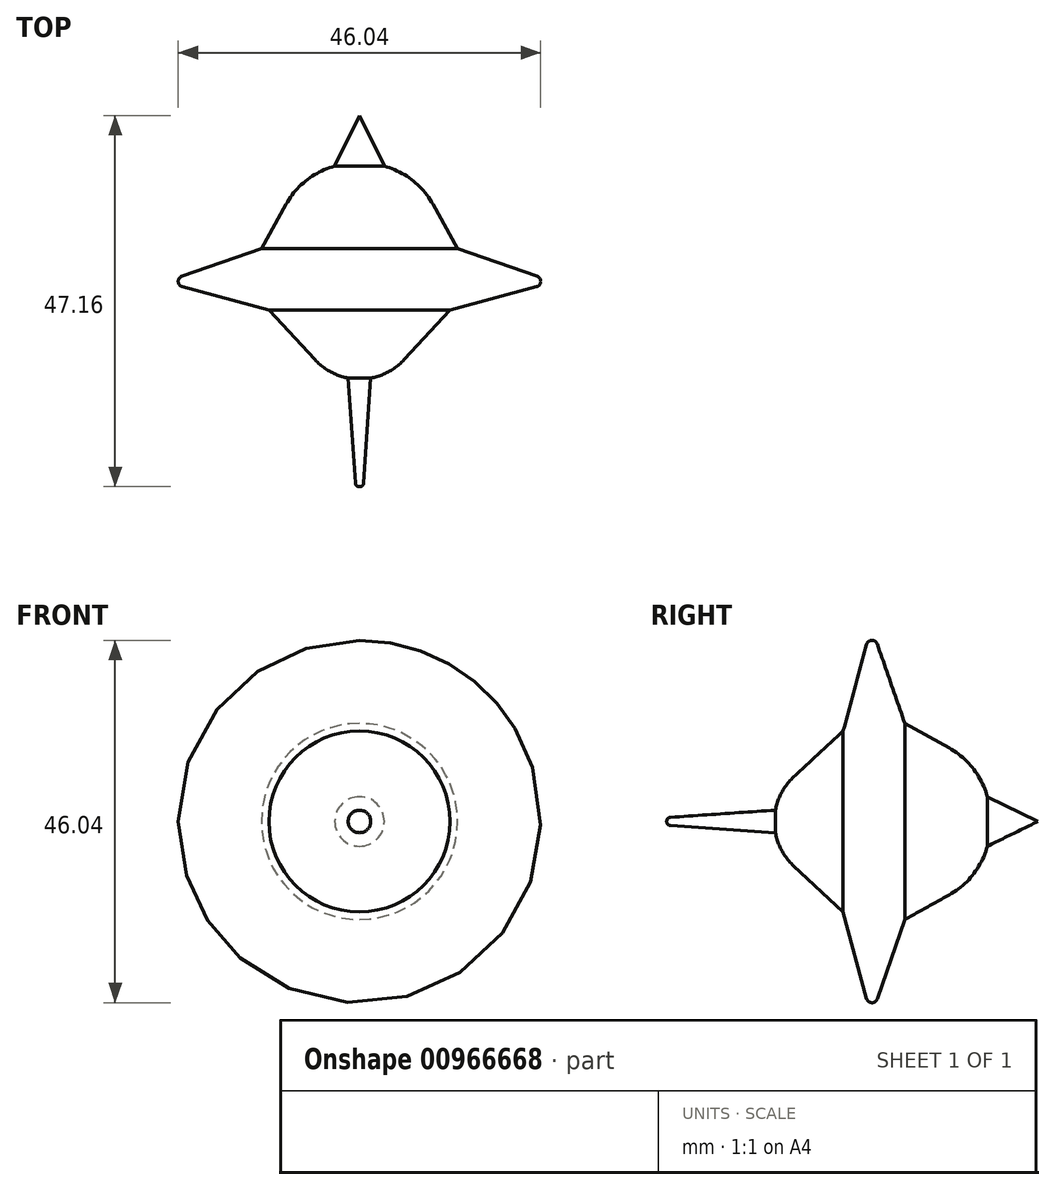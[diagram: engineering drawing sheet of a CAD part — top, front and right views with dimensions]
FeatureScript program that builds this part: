
annotation { "Feature Type Name" : "Feature", "Feature Type Description" : "" }
export const myFeature = defineFeature(function(context is Context, id is Id, definition is map)
    precondition{}
    {
        {
            var Q0;
            Q0=qCreatedBy(makeId("Right.planeOp"),FACE);
            var sketch = newSketch(context, id + "F0", { "sketchPlane" : qUnion([Q0])});
            skArc(sketch, "E0.cCircle", {"start": v(-12.08, 0) * mm, "mid": v(0, -12.08) * mm, "end": v(12.08, 0) * mm, "construction": true});
            skLineSegment(sketch, "E0.0", {"start": v(13.54, -6.3) * mm, "end": v(2.46, -12.46) * mm});
            skLineSegment(sketch, "E0.1", {"start": v(-5.38, -11.5) * mm, "end": v(-14.66, -2.87) * mm});
            skLineSegment(sketch, "E0.2", {"start": v(-14.66, -2.87) * mm, "end": v(-14, -1.43) * mm});
            skLineSegment(sketch, "E0.4", {"start": v(12.93, -3.15) * mm, "end": v(13.54, -6.3) * mm});
            skPoint(sketch, "E0.0.midPoint", {"position": v(5.87, -10.56) * mm});
            skLineSegment(sketch, "E1", {"start": v(28.59, 0) * mm, "end": v(-32.16, 0) * mm});
            skPoint(sketch, "E2.orphan", {"position": v(-7.26, 13.06) * mm});
            skPoint(sketch, "E3.orphan", {"position": v(10.18, 10.93) * mm});
            skLineSegment(sketch, "E4", {"start": v(12.93, -3.15) * mm, "end": v(19.36, 0) * mm});
            skPoint(sketch, "E5.orphan", {"position": v(12.31, 0) * mm});
            skLineSegment(sketch, "E6", {"start": v(-5.38, -11.5) * mm, "end": v(-1.8, -24.7) * mm});
            skLineSegment(sketch, "E7", {"start": v(-1.8, -24.7) * mm, "end": v(2.46, -12.46) * mm});
            skLineSegment(sketch, "E8", {"start": v(-1.8, -14.83) * mm, "end": v(-1.8, -35.61) * mm, "construction": true});
            skLineSegment(sketch, "E9", {"start": v(-14, -1.43) * mm, "end": v(-27.8, -0.5) * mm});
            skLineSegment(sketch, "E10", {"start": v(-27.8, -0.5) * mm, "end": v(-27.8, 0) * mm});
            skPoint(sketch, "E11.orphan", {"position": v(-13.33, 0) * mm});
            skSolve(sketch);
        }
        {
            var Q0;
            Q0=makeQuery(id+"F0.imprint","IMPRINT",FACE,{"disambiguationData":[TD([[makeQuery(id+"F0.imprint","IMPRINT",EDGE,{"derivedFrom":sQuery(id+"F0.wireOp",EDGE,"E0.0")}),-1.0]])]});
            var Q1;
            Q1=sQuery(id+"F0.wireOp",EDGE,"E1");
            revolve(context, id + "F1", {"surfaceOperationType" : NewSurfaceOperationType.NEW, "entities" : qUnion([Q0]), "axis" : qUnion([Q1]), "revolveType" : RevolveType.FULL});
        }
        {
            var Q0;
            Q0=makeQuery(id+"F1.opRevolve","SWEPT_EDGE",EDGE,{"disambiguationData":[OSD([sQuery(id+"F0.wireOp",EDGE,"E6"),sQuery(id+"F0.wireOp",EDGE,"E7")])]});
            fillet(context, id + "F2", {"entities" : qUnion([Q0]), "radius" : 0.7 * mm, "tangentPropagation" : true, "allowEdgeOverflow" : false});
        }
        {
            var Q0;
            Q0=makeQuery(id+"F1.opRevolve","SWEPT_EDGE",EDGE,{"disambiguationData":[OSD([sQuery(id+"F0.wireOp",EDGE,"E0.0"),sQuery(id+"F0.wireOp",EDGE,"E0.4")])]});
            fillet(context, id + "F3", {"entities" : qUnion([Q0]), "radius" : 10.1 * mm, "tangentPropagation" : true, "allowEdgeOverflow" : false});
        }
        {
            var Q0;
            Q0=makeQuery(id+"F1.opRevolve","SWEPT_EDGE",EDGE,{"disambiguationData":[OSD([sQuery(id+"F0.wireOp",EDGE,"E0.1"),sQuery(id+"F0.wireOp",EDGE,"E0.2")])]});
            fillet(context, id + "F4", {"entities" : qUnion([Q0]), "radius" : 7.7 * mm, "tangentPropagation" : true, "allowEdgeOverflow" : false});
        }
        {
            var Q0;
            Q0=makeQuery(id+"F1.opRevolve","SWEPT_EDGE",EDGE,{"disambiguationData":[OSD([sQuery(id+"F0.wireOp",EDGE,"E9"),sQuery(id+"F0.wireOp",EDGE,"E10")])]});
            fillet(context, id + "F5", {"entities" : qUnion([Q0]), "radius" : 0.5 * mm, "tangentPropagation" : true, "allowEdgeOverflow" : false});
        }
    });
